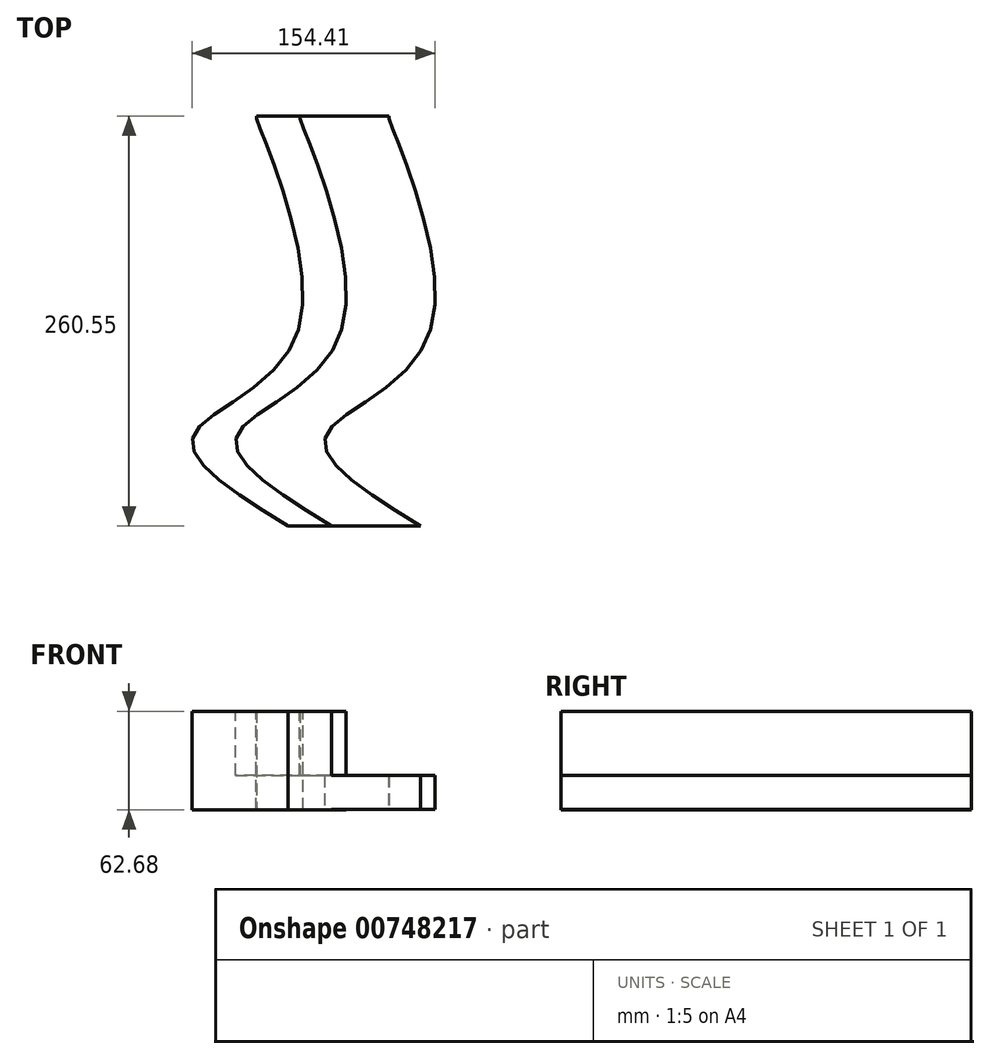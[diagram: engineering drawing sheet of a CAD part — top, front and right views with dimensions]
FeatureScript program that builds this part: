
annotation { "Feature Type Name" : "Feature", "Feature Type Description" : "" }
export const myFeature = defineFeature(function(context is Context, id is Id, definition is map)
    precondition{}
    {
        {
            var Q0;
            Q0=qCreatedBy(makeId("Front.planeOp"),FACE);
            var sketch = newSketch(context, id + "F0", { "sketchPlane" : qUnion([Q0])});
            skLineSegment(sketch, "E0.bottom", {"start": v(-44.27, 29.65) * mm, "end": v(-16.72, 29.65) * mm});
            skLineSegment(sketch, "E0.top", {"start": v(-44.27, -33.03) * mm, "end": v(-16.72, -33.03) * mm});
            skLineSegment(sketch, "E0.left", {"start": v(-44.27, 29.65) * mm, "end": v(-44.27, -33.03) * mm});
            skLineSegment(sketch, "E0.right", {"start": v(-16.72, 29.65) * mm, "end": v(-16.72, -11.1) * mm});
            skLineSegment(sketch, "E1.bottom", {"start": v(-16.72, -11.1) * mm, "end": v(39.77, -11.1) * mm});
            skLineSegment(sketch, "E1.top", {"start": v(-16.72, -32.75) * mm, "end": v(39.77, -32.75) * mm});
            skLineSegment(sketch, "E1.right", {"start": v(39.77, -11.1) * mm, "end": v(39.77, -32.75) * mm});
            skLineSegment(sketch, "E2.trimOffspring", {"start": v(-16.72, -32.75) * mm, "end": v(-16.72, -33.03) * mm});
            skSolve(sketch);
        }
        {
            var Q0;
            Q0=qCreatedBy(makeId("Top.planeOp"),FACE);
            var sketch = newSketch(context, id + "F1", { "sketchPlane" : qUnion([Q0])});
            skFitSpline(sketch, "E3", {"points": [v(45.96, -105.82) * mm, v(-14.48, -49.05) * mm, v(52.42, 18.97) * mm, v(25.72, 154.45) * mm, v(26, 154.73) * mm], "startDerivative": vector(-338.4, 209.7) * mm, "endDerivative": vector(19.82, 2.53) * mm});
            skSolve(sketch);
        }
        {
            var Q0;
            Q0=makeQuery(id+"F0.imprint","IMPRINT",FACE,{"disambiguationData":[TD([[makeQuery(id+"F0.imprint","IMPRINT",EDGE,{"derivedFrom":sQuery(id+"F0.wireOp",EDGE,"E0.bottom")}),-1.0]])]});
            var Q1;
            Q1=sQuery(id+"F1.wireOp",EDGE,"E3");
            sweep(context, id + "F2", {"profiles" : qUnion([Q0]), "path" : qUnion([Q1]), "keepProfileOrientation" : true});
        }
    });
